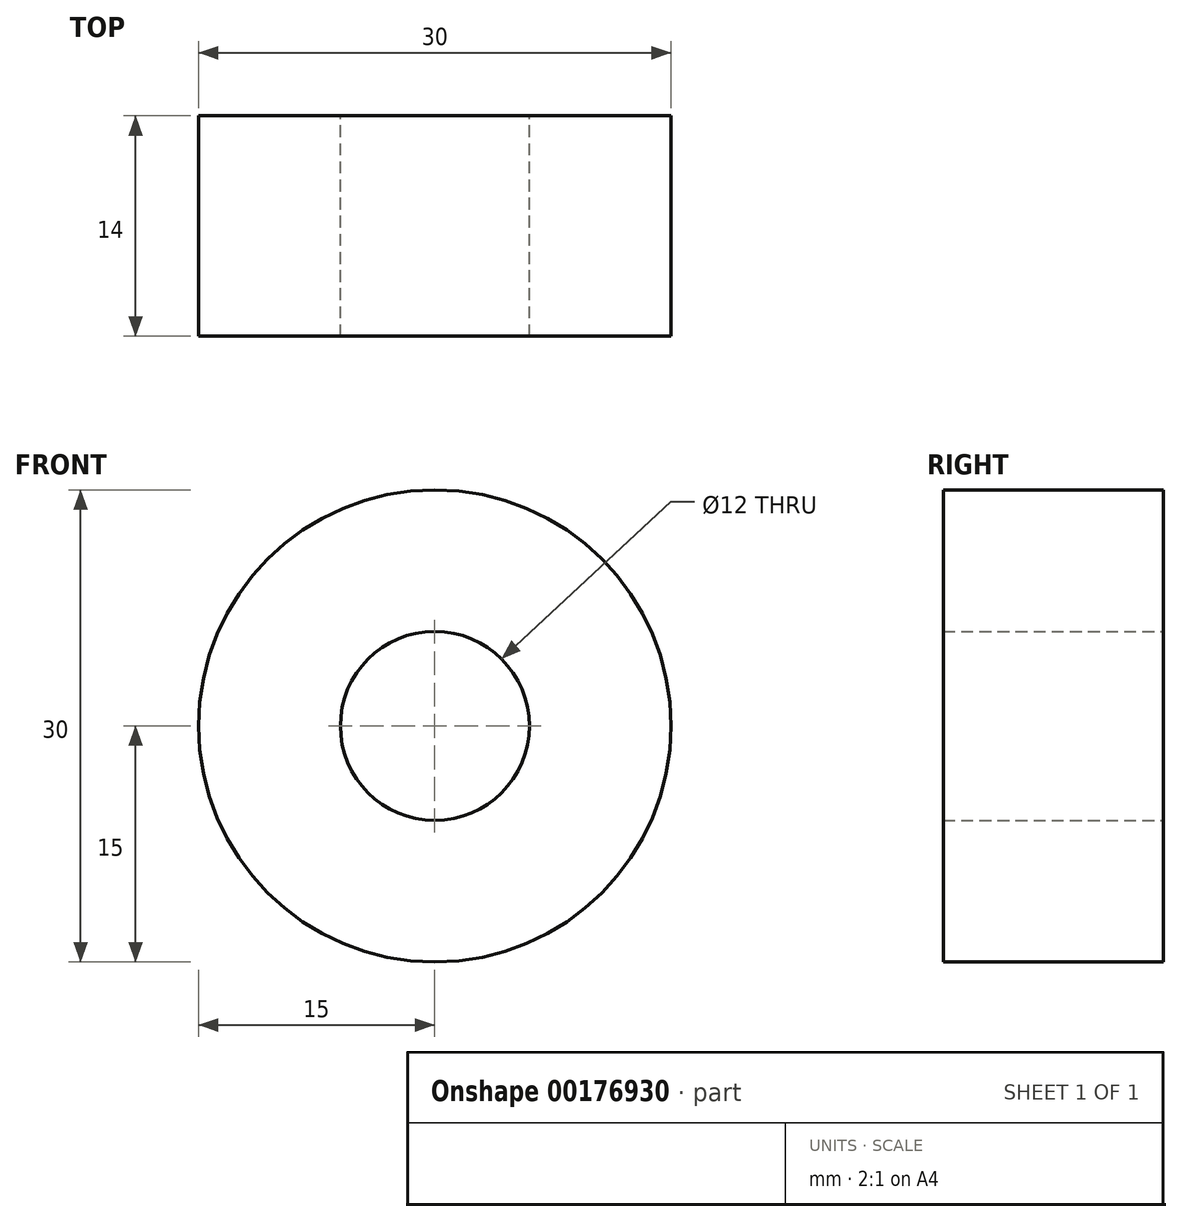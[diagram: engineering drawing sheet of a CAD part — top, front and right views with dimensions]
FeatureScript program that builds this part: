
annotation { "Feature Type Name" : "Feature", "Feature Type Description" : "" }
export const myFeature = defineFeature(function(context is Context, id is Id, definition is map)
    precondition{}
    {
        {
            var Q0;
            Q0=qCreatedBy(makeId("Front.planeOp"),FACE);
            var sketch = newSketch(context, id + "F0", { "sketchPlane" : qUnion([Q0])});
            skCircle(sketch, "E0", {"center": v(0, 0) * mm, "radius": 15 * mm});
            skCircle(sketch, "E1", {"center": v(0, 0) * mm, "radius": 6 * mm});
            skSolve(sketch);
        }
        {
            var Q0;
            Q0=makeQuery(id+"F0.imprint","IMPRINT",FACE,{"disambiguationData":[TD([[makeQuery(id+"F0.imprint","IMPRINT",EDGE,{"derivedFrom":sQuery(id+"F0.wireOp",EDGE,"E0")}),1.0]])]});
            extrude(context, id + "F1", {"entities" : qUnion([Q0]), "depth" : 14 * mm});
        }
    });
